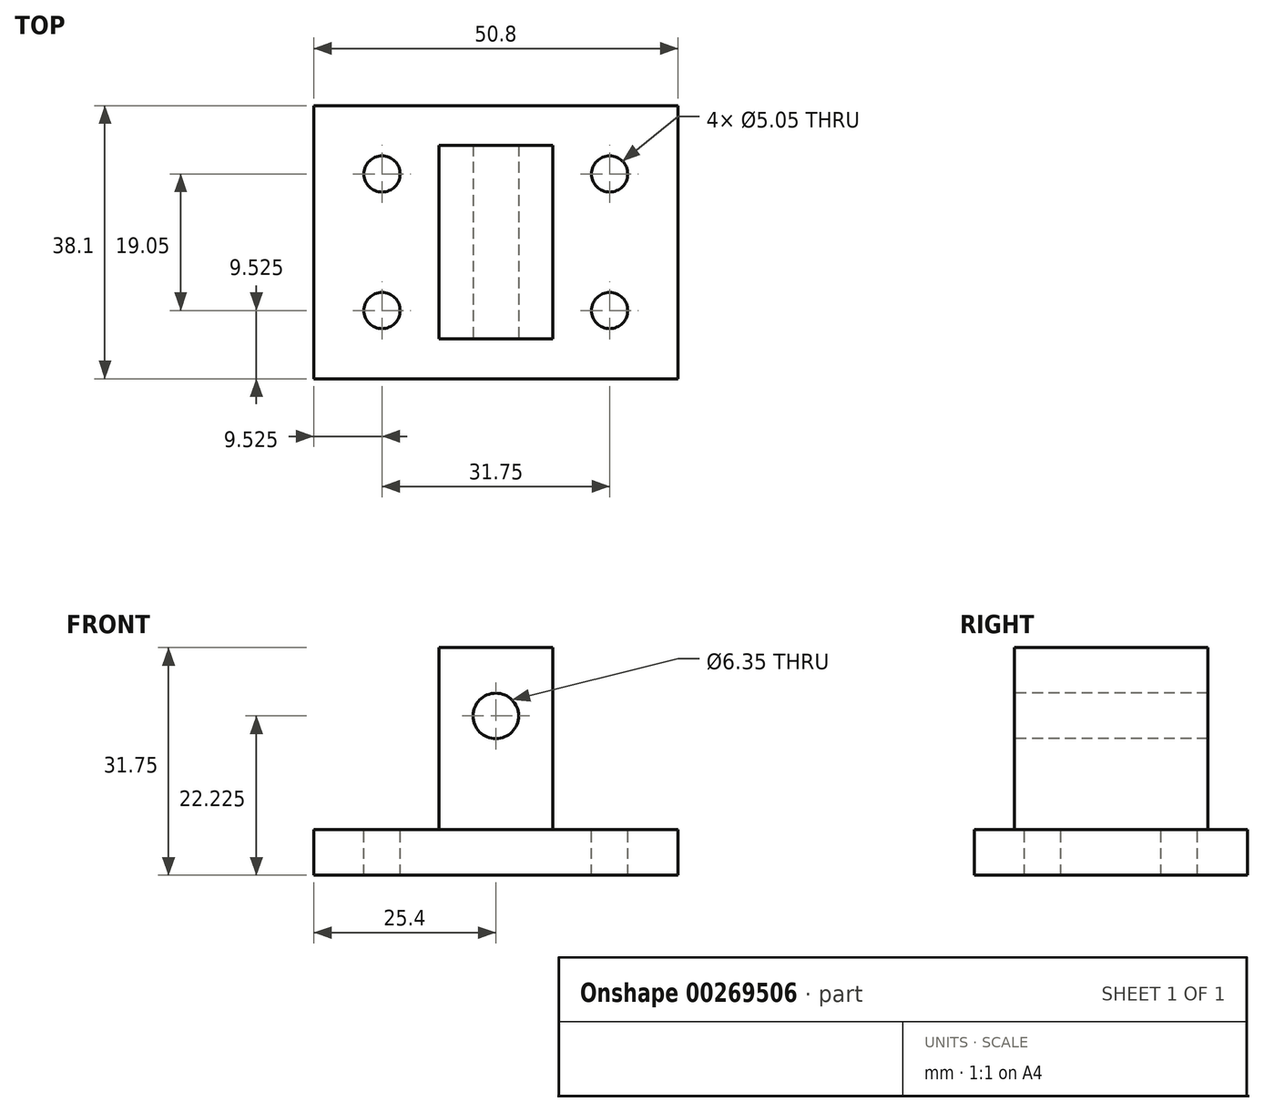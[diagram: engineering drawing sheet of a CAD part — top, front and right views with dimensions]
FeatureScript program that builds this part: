
annotation { "Feature Type Name" : "Feature", "Feature Type Description" : "" }
export const myFeature = defineFeature(function(context is Context, id is Id, definition is map)
    precondition{}
    {
        {
            var Q0;
            Q0=qCreatedBy(makeId("Top.planeOp"),FACE);
            var sketch = newSketch(context, id + "F0", { "sketchPlane" : qUnion([Q0])});
            skLineSegment(sketch, "E0.bottom", {"start": v(25.4, 19.05) * mm, "end": v(-25.4, 19.05) * mm});
            skLineSegment(sketch, "E0.top", {"start": v(25.4, -19.05) * mm, "end": v(-25.4, -19.05) * mm});
            skLineSegment(sketch, "E0.left", {"start": v(25.4, 19.05) * mm, "end": v(25.4, -19.05) * mm});
            skLineSegment(sketch, "E0.right", {"start": v(-25.4, 19.05) * mm, "end": v(-25.4, -19.05) * mm});
            skPoint(sketch, "E0.middle", {"position": v(0, 0) * mm});
            skSolve(sketch);
        }
        {
            var Q0;
            Q0 = qSketchRegion(id + "F0", true);
            extrude(context, id + "F1", {"entities" : qUnion([Q0]), "depth" : 6.35 * mm, "offsetDistance" : 25.4 * mm});
        }
        {
            var Q0;
            Q0=makeQuery(id+"F1.opExtrude","CAP_FACE",FACE,{"disambiguationData":[OSD([sQuery(id+"F0.wireOp",EDGE,"E0.bottom"),sQuery(id+"F0.wireOp",EDGE,"E0.top"),sQuery(id+"F0.wireOp",EDGE,"E0.left"),sQuery(id+"F0.wireOp",EDGE,"E0.right")])],"isStart":false});
            var sketch = newSketch(context, id + "F2", { "sketchPlane" : qUnion([Q0])});
            skLineSegment(sketch, "E1.bottom", {"start": v(7.94, 13.5) * mm, "end": v(-7.94, 13.5) * mm});
            skLineSegment(sketch, "E1.top", {"start": v(7.94, -13.5) * mm, "end": v(-7.94, -13.5) * mm});
            skLineSegment(sketch, "E1.left", {"start": v(7.94, 13.5) * mm, "end": v(7.94, -13.5) * mm});
            skLineSegment(sketch, "E1.right", {"start": v(-7.94, 13.5) * mm, "end": v(-7.94, -13.5) * mm});
            skPoint(sketch, "E1.middle", {"position": v(0, 0) * mm});
            skSolve(sketch);
        }
        {
            var Q0;
            Q0 = qSketchRegion(id + "F2", true);
            extrude(context, id + "F3", {"entities" : qUnion([Q0]), "operationType" : NewBodyOperationType.ADD, "depth" : 25.4 * mm, "offsetDistance" : 25.4 * mm});
        }
        {
            var Q0;
            Q0=makeQuery(id+"F3.opExtrude","SWEPT_FACE",FACE,{"disambiguationData":[OSD([sQuery(id+"F2.wireOp",EDGE,"E1.top")])]});
            var sketch = newSketch(context, id + "F4", { "sketchPlane" : qUnion([Q0])});
            skCircle(sketch, "E2", {"center": v(0, 22.23) * mm, "radius": 3.18 * mm});
            skSolve(sketch);
        }
        {
            var Q0;
            Q0 = qSketchRegion(id + "F4", true);
            extrude(context, id + "F5", {"entities" : qUnion([Q0]), "operationType" : NewBodyOperationType.REMOVE, "endBound" : BoundingType.THROUGH_ALL, "oppositeDirection" : true, "depth" : 25.4 * mm, "offsetDistance" : 25.4 * mm});
        }
        {
            var Q0;
            Q0=makeQuery(id+"F1.opExtrude","CAP_FACE",FACE,{"disambiguationData":[OSD([sQuery(id+"F0.wireOp",EDGE,"E0.bottom"),sQuery(id+"F0.wireOp",EDGE,"E0.top"),sQuery(id+"F0.wireOp",EDGE,"E0.left"),sQuery(id+"F0.wireOp",EDGE,"E0.right")])],"isStart":false});
            var sketch = newSketch(context, id + "F6", { "sketchPlane" : qUnion([Q0])});
            skLineSegment(sketch, "E3.bottom", {"start": v(15.88, 9.53) * mm, "end": v(-15.88, 9.53) * mm});
            skLineSegment(sketch, "E3.top", {"start": v(15.88, -9.53) * mm, "end": v(-15.88, -9.53) * mm});
            skLineSegment(sketch, "E3.left", {"start": v(15.88, 9.53) * mm, "end": v(15.88, -9.53) * mm});
            skLineSegment(sketch, "E3.right", {"start": v(-15.88, 9.53) * mm, "end": v(-15.88, -9.53) * mm});
            skPoint(sketch, "E3.middle", {"position": v(0, 0) * mm});
            skSolve(sketch);
        }
        {
            var Q0;
            Q0=sQuery(id+"F6.wireOp",VERTEX,"E3.right.start");
            var Q1;
            Q1=sQuery(id+"F6.wireOp",VERTEX,"E3.right.end");
            var Q2;
            Q2=sQuery(id+"F6.wireOp",VERTEX,"E3.left.start");
            var Q3;
            Q3=sQuery(id+"F6.wireOp",VERTEX,"E3.top.start");
            var Q4;
            Q4=makeQuery(id+"F1.opExtrude","SWEPT_BODY",BODY,{"disambiguationData":[OSD([sQuery(id+"F0.wireOp",EDGE,"E0.bottom"),sQuery(id+"F0.wireOp",EDGE,"E0.top"),sQuery(id+"F0.wireOp",EDGE,"E0.left"),sQuery(id+"F0.wireOp",EDGE,"E0.right")])]});
            hole(context, id + "F7", {"style" : HoleStyle.SIMPLE, "endStyle" : HoleEndStyle.THROUGH, "standardTappedOrClearance" : lookupTablePath({ "standard" : "ANSI", "size" : "#8 (0.2)", "type" : "Drilled" }), "standardBlindInLast" : lookupTablePath({ "standard" : "ANSI", "size" : "#8", "type" : "Drilled" }), "holeDiameter" : 5.05 * mm, "majorDiameter" : 6.35 * mm, "tappedDepth" : 10.3 * mm, "tapClearance" : 3, "locations" : qUnion([Q0, Q1, Q2, Q3]), "scope" : qUnion([Q4])});
        }
    });
